# Revit family: Edelstahlrohrschelle V4A, ohne AG, ohne VS, Ø321- 410, Gummi
name_source: partatom
category: HLS-Bauteile
revit_build: Autodesk Revit 2017 (Build: 20190507_1515(x64)
units: mm (PartAtom-declared; Revit-internal decimal feet)

## family parameters
Arbeitsebenenbasiert = Ja
Beim Laden mit Abzugskörper schneiden = Nein
Bemaßung runder Anschluss = Durchmesser verwenden
Gemeinsam genutzt = Ja
Immer vertikal = Nein
Raumberechnungspunkt = Nein
Teiletyp = Normal

## types (4) — shared parameters
A = 11 mm  [stored 0.0360892 ft]
Anschluss = ohne Anschluss
Bauart = zweiteilig
Baustoffklasse = B2
DF1 = 32 mm  [stored 0.104987 ft]
DF2 = 34 mm
DS = 6 mm  [stored 0.019685 ft]
DVS = 17 mm
Dämmstärke = 6 mm  [stored 0.019685 ft]
Fabrikat = MEFA
Farbe Schalldämmeinlage = schwarz
Firma = MEFA Befestigungs- und Montagesysteme GmbH
Kurztext1 = Rohrschelle Edelstahl V4A 50x5,0
MB = 50 mm  [stored 0.164042 ft]
MD = 5 mm  [stored 0.0164042 ft]
Material = Edelstahl
Material Schalldämmeinlage = TPE
Materialmaße = 50x5,0 mm
Mengeneinheit = St
Rohraußendurchmesser Zoll = Zoll
Schalldämmeinlage = Gummi
Verschluss = Schraubenverschluss
Vorgabe-Ansicht = 1219 mm
max. Temperaturbeständigkeit = 100 °C
max. zul. Last horizontal = 0.00 kN
max. zul. Last vertikal = 0.00 kN
vpe = 1 St
zero-valued in all types: HGA, Nennweite DN Rohr, Rohraußendurchmesser, Stärke Material

## per-type parameters (varying)
| type | AB | Achsabstand | Artikelnummer | B | D | D0 | Dmax | Dmin | EAN | Gewicht | Gewicht pro Bauteil | H | Kurztext2 | R | RM | S | max. Rohraußendurchmesser | min. Rohraußendurchmesser |
| Edelstahlrohrschelle V4A, o.AG, o.VS, Ø321-325, Gummi | 4 mm  [stored 0.0131234 ft] | 382 mm | 0494046 | 413 mm | 325 mm  [stored 1.06627 ft] | 337 mm  [stored 1.10564 ft] | 325 mm  [stored 1.06627 ft] | 321 mm  [stored 1.05315 ft] | 4250928413376 | 2.51 kg | 2.51 kg | 347 mm  [stored 1.13845 ft] | 321 - 325 mm ohne Anschluss TPE | 169 mm | 174 mm | 381 mm  [stored 1.25 ft] | 325 mm  [stored 1.06627 ft] | 321 mm  [stored 1.05315 ft] |
| Edelstahlrohrschelle V4A, o.AG, o.VS, Ø351-360, Gummi | 9 mm | 416 mm | 0494051 | 448 mm | 360 mm  [stored 1.1811 ft] | 372 mm | 360 mm  [stored 1.1811 ft] | 351 mm  [stored 1.15157 ft] | 4250928413383 | 2.71 kg | 2.71 kg | 382 mm  [stored 1.25328 ft] | 351 - 360 mm ohne Anschluss TPE | 186 mm  [stored 0.610236 ft] | 191 mm  [stored 0.62664 ft] | 416 mm  [stored 1.36483 ft] | 360 mm  [stored 1.1811 ft] | 351 mm  [stored 1.15157 ft] |
| Edelstahlrohrschelle V4A, o.AG, o.VS, Ø361-370, Gummi | 9 mm | 426 mm | 0494052 | 458 mm  [stored 1.50262 ft] | 370 mm  [stored 1.21391 ft] | 382 mm  [stored 1.25328 ft] | 370 mm  [stored 1.21391 ft] | 361 mm  [stored 1.18438 ft] | 4250928413390 | 2.78 kg | 2.78 kg | 392 mm  [stored 1.28609 ft] | 361 - 370 mm ohne Anschluss TPE | 191 mm  [stored 0.62664 ft] | 196 mm  [stored 0.643045 ft] | 426 mm  [stored 1.39764 ft] | 370 mm  [stored 1.21391 ft] | 361 mm  [stored 1.18438 ft] |
| Edelstahlrohrschelle V4A, o.AG, o.VS, Ø401-410, Gummi | 9 mm | 466 mm | 0494056 | 498 mm | 410 mm  [stored 1.34514 ft] | 422 mm | 410 mm  [stored 1.34514 ft] | 401 mm  [stored 1.31562 ft] | 4250928413406 | 3.05 kg | 3.05 kg | 432 mm  [stored 1.41732 ft] | 401 - 410 mm ohne Anschluss TPE | 211 mm | 216 mm  [stored 0.708661 ft] | 466 mm  [stored 1.52887 ft] | 410 mm  [stored 1.34514 ft] | 401 mm  [stored 1.31562 ft] |

note: [stored X ft] marks values corroborated as IEEE doubles in the binary element streams (Revit-internal decimal feet)
